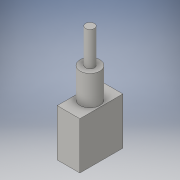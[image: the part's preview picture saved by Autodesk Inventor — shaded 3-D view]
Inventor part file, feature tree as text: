
AUTODESK INVENTOR PART (.ipt)
format: ipt  version: 2016 (Build 200138000, 138)  size: 104,960 bytes
history: native  units: in
note: dims shown in document units (in); Inventor stores cm internally (conversion verified against a paired STEP export)
features: extrude x3, sketch x3
ambient origin geometry x8: Origin, YZ Plane, XZ Plane, XY Plane, X Axis, Y Axis, Z Axis, Center Point
bodies: Solid1 (feature_tree)
feature tree (6):
  extrude  "Extrusion1"  Depth=0.5in
  extrude  "Extrusion2"  Depth=0.5472in
  extrude  "Extrusion3"  Depth=0.3976in
  sketch  "Sketch1"  dims[d0=0.2638in d1=0.5in]
  sketch  "Sketch2"  dims[d2=0.5472in d3=0.0in d4=0.2307in]
  sketch  "Sketch3"  dims[d5=0.3465in d6=0.0in d7=0.1024in d8=0.3976in d9=0.0in]
